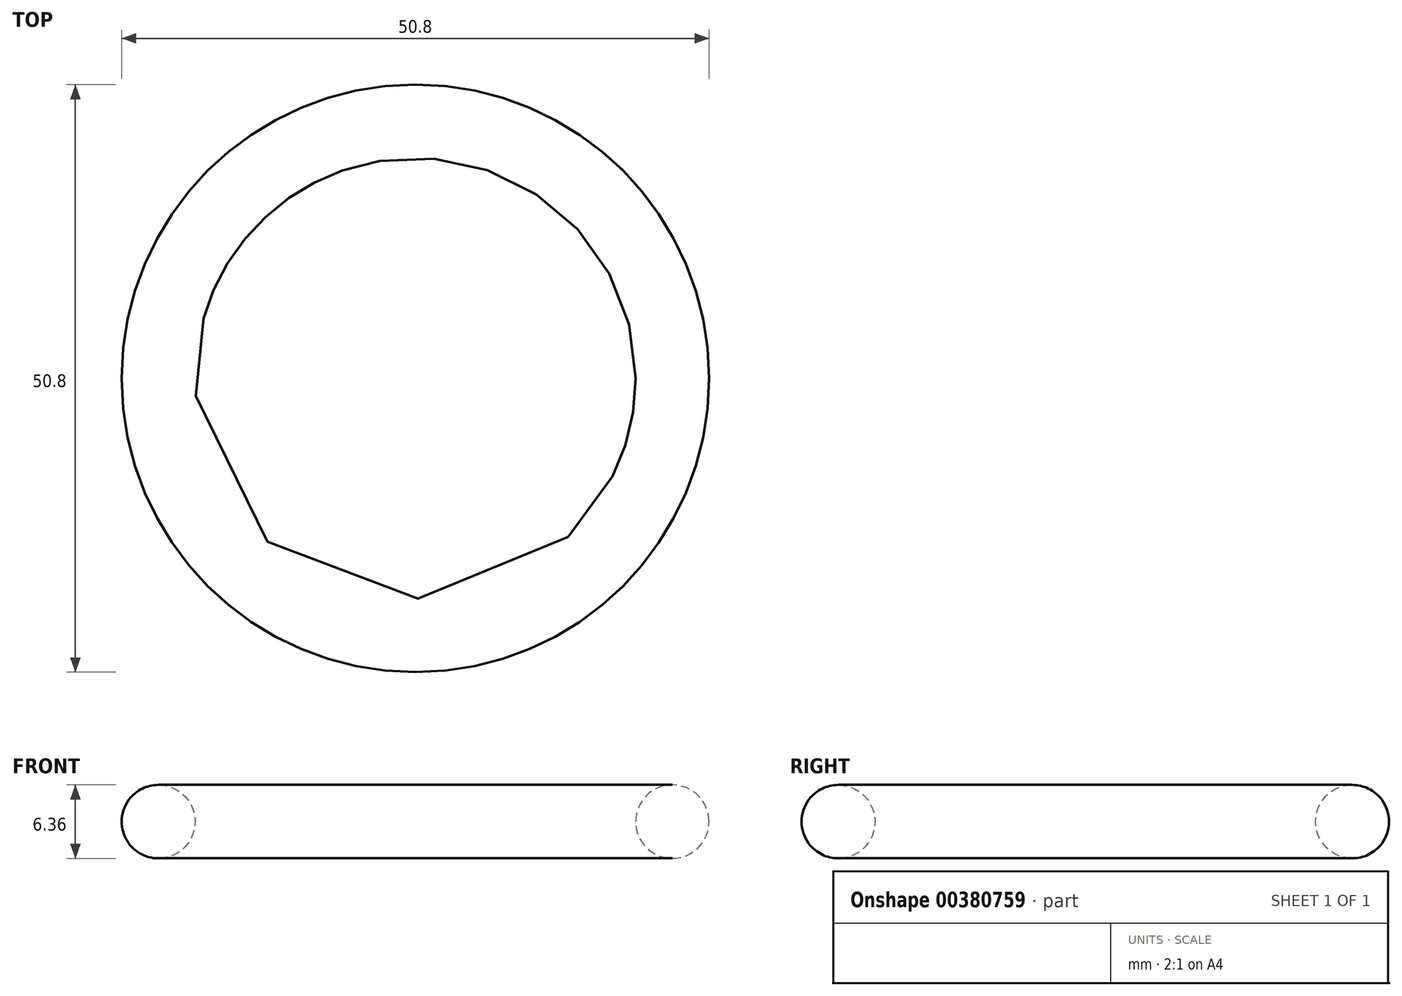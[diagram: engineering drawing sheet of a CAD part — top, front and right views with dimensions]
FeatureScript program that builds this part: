
annotation { "Feature Type Name" : "Feature", "Feature Type Description" : "" }
export const myFeature = defineFeature(function(context is Context, id is Id, definition is map)
    precondition{}
    {
        {
            var Q0;
            Q0=qCreatedBy(makeId("Front.planeOp"),FACE);
            var sketch = newSketch(context, id + "F0", { "sketchPlane" : qUnion([Q0])});
            skCircle(sketch, "E0", {"center": v(-22.23, 0) * mm, "radius": 3.18 * mm});
            skLineSegment(sketch, "E1", {"start": v(0, 13.38) * mm, "end": v(0, -9.53) * mm, "construction": true});
            skSolve(sketch);
        }
        {
            var Q0;
            Q0 = qSketchRegion(id + "F0", true);
            var Q1;
            Q1=sQuery(id+"F0.wireOp",EDGE,"E1");
            revolve(context, id + "F1", {"entities" : qUnion([Q0]), "axis" : qUnion([Q1]), "revolveType" : RevolveType.FULL});
        }
    });
